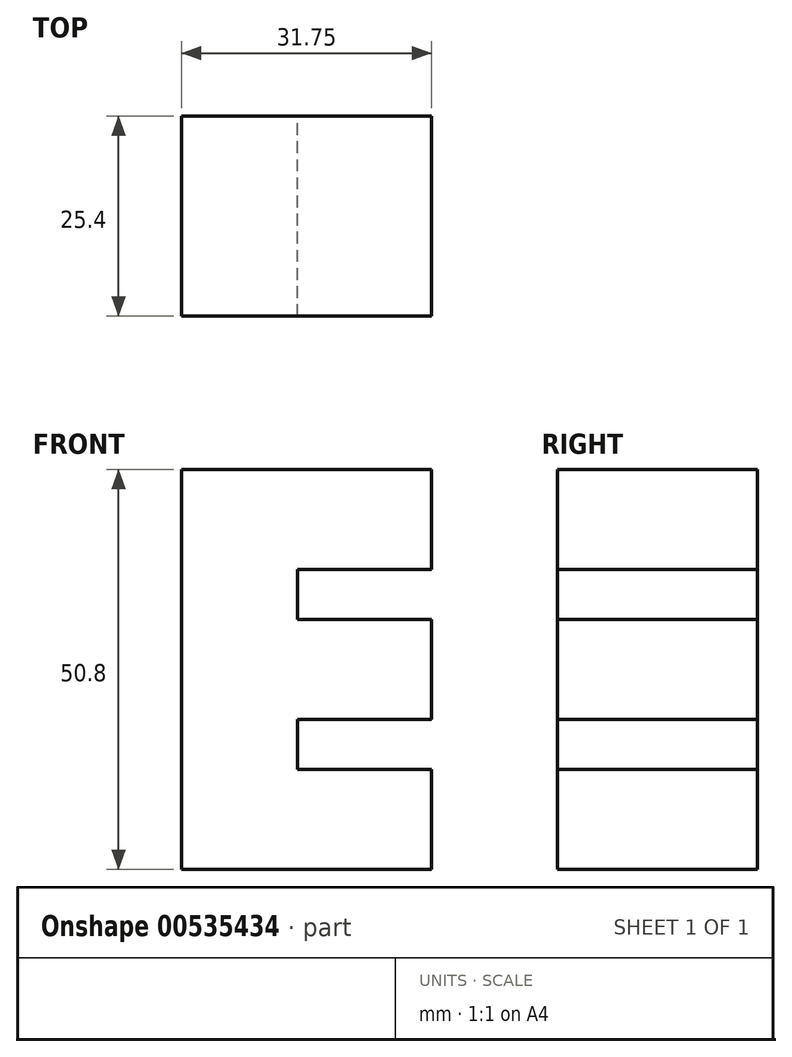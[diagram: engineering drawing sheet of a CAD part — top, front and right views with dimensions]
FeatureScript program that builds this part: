
annotation { "Feature Type Name" : "Feature", "Feature Type Description" : "" }
export const myFeature = defineFeature(function(context is Context, id is Id, definition is map)
    precondition{}
    {
        {
            var Q0;
            Q0=qCreatedBy(makeId("Front.planeOp"),FACE);
            var sketch = newSketch(context, id + "F0", { "sketchPlane" : qUnion([Q0])});
            skLineSegment(sketch, "E0", {"start": v(-60.9, 50.8) * mm, "end": v(-60.9, 0) * mm});
            skLineSegment(sketch, "E1", {"start": v(-60.9, 0) * mm, "end": v(-29.15, 0) * mm});
            skLineSegment(sketch, "E2", {"start": v(-29.15, 0) * mm, "end": v(-29.15, 12.7) * mm});
            skLineSegment(sketch, "E3", {"start": v(-29.15, 12.7) * mm, "end": v(-46.18, 12.7) * mm});
            skLineSegment(sketch, "E4", {"start": v(-46.18, 12.7) * mm, "end": v(-46.18, 19.05) * mm});
            skLineSegment(sketch, "E5", {"start": v(-46.18, 19.05) * mm, "end": v(-29.15, 19.05) * mm});
            skLineSegment(sketch, "E6", {"start": v(-29.15, 19.05) * mm, "end": v(-29.15, 31.75) * mm});
            skLineSegment(sketch, "E7", {"start": v(-29.15, 31.75) * mm, "end": v(-46.18, 31.75) * mm});
            skLineSegment(sketch, "E8", {"start": v(-46.18, 31.75) * mm, "end": v(-46.18, 38.1) * mm});
            skLineSegment(sketch, "E9", {"start": v(-46.18, 38.1) * mm, "end": v(-29.15, 38.1) * mm});
            skLineSegment(sketch, "E10", {"start": v(-60.9, 50.8) * mm, "end": v(-29.15, 50.8) * mm});
            skLineSegment(sketch, "E11", {"start": v(-29.15, 38.1) * mm, "end": v(-29.15, 50.8) * mm});
            skSolve(sketch);
        }
        {
            var Q0;
            Q0=makeQuery(id+"F0.imprint","IMPRINT",FACE,{"disambiguationData":[TD([[makeQuery(id+"F0.imprint","IMPRINT",EDGE,{"derivedFrom":sQuery(id+"F0.wireOp",EDGE,"E0")}),1.0]])]});
            extrude(context, id + "F1", {"entities" : qUnion([Q0]), "depth" : 25.4 * mm, "offsetDistance" : 25.4 * mm});
        }
    });
